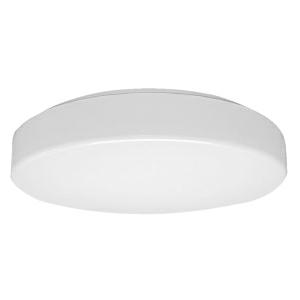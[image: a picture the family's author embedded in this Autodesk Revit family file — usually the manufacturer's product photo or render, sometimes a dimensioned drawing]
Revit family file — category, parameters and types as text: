
# Revit family: oblo_fit_-_oba_4000_830_00813352_90a0
name_source: partatom
category: Lighting Fixtures
units: mm (PartAtom-declared; Revit-internal decimal feet)

## family parameters
Cut with Voids When Loaded = No
Host = Face
Light Source = No
Part Type = Normal
Room Calculation Point = No
Round Connector Dimension = Use Diameter
Shared = No

## types (1)
- deko (1 x LED, 3350 lm, 3000K)
    Apparent Load = 44 VA
    Approval mark = CE
    CIE Flux Codes = 47 78 95 100 100
    Color Rendering = 80-89
    Color Temperature = 3000K
    Control Gear = Electronic ballast
    Default Elevation = 1800 mm
    Description = OBA 4000/830|Surface-mounted luminaire.|light source:   Warm white   |work equipment: Power supply unit|luminous flux: 4300 lm|light distribution: Direct|class of protection: I|technology: Switchable|mains lead: Direct power supply|glare control: without|
    Frequency = 50 Hz, 60 Hz
    Height = 95 mm
    Lamp = 1 x LED
    Lamp Light Flux = 3350 lm
    Lamp count = 1
    Length = 460 mm
    Luminous efficacy = 76 lm/W
    Manufacturer = Waldmann
    ModVariant = No
    Model = 00813352
    Mounting Place = Ceiling
    Mounting Type = Surface mounted
    Number of Poles = 1
    OnlyDefault = Yes
    Power Factor = 1
    Product Name = OBLO.fit - OBA 4000/830
    Product group = Ceiling mounted luminaire
    ProductGroupID = 3
    Protection Class = Protection class I
    Protection Degree = IP 40
    RLX_Detail_Level = 1
    RLX_Emergency_Light_Flux = 0 lm
    RLX_Emergency_Type = 0
    RLX_Emergency_Type_DB = No
    RlxData = <blob elided: 23445 chars, md5=5971358b>
    Socket = socket
    Standby Power = 0 W
    System Light Flux = 3350 lm
    System Power = 44 W
    Type Comments = mit Deko-Ring
    Type Image = oblo_led.jpg
    URL = http://relux.com
    VarID = deko
    Voltage = 230 V
    Voltage Range = 220-240 V
    Weight = 0.00 kg
    Width = 0 mm  [stored 0 ft]

note: [stored X ft] marks values corroborated as IEEE doubles in the binary element streams (Revit-internal decimal feet)

## geometry (parser evidence)
native form markers: Blend x4, Sweep x10
no freeform markers — native parametric forms only
